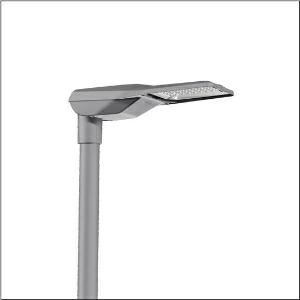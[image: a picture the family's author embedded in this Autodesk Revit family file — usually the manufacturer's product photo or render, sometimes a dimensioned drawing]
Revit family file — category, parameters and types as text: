
# Revit family: streetlight_sl_21_iq_mini___st0_5a_5xe2b41g08gb_465e
name_source: partatom
category: Lighting Fixtures
units: mm (PartAtom-declared; Revit-internal decimal feet)

## family parameters
Cut with Voids When Loaded = No
Host = Face
Light Source = No
Part Type = Normal
Room Calculation Point = No
Round Connector Dimension = Use Diameter
Shared = No

## types (1)
- --- (1 x LED, 5920 lm, 37.1 W, 4000K)
    Apparent Load = 37 VA
    CIE Flux Codes = 41 75 97 100 100
    Color Rendering = 70
    Color Temperature = 4000K
    Default Elevation = 1800 mm
    Description = Streetlight SL 21 iQ mini, mast luminaire, primary light control with lens, of PMMA, primary optical cover: cover, of toughened safety glass, transparent, light distribution: ST0.5a, light emission: direct distribution, primary light characteristic: asymmetric, installation type: post-top, side-entry, LED, High Power LED, rated luminous flux: 5.920lm, luminous efficacy: 160lm/W, light colour: 740, colour temperature: 4000K, control: Street-Remote, Auto-Match, Temp-Guard, Lumen-Switch, Night-Set, Smart-Wire, Light-Fading, Desk-Remote (wireless, voltage-free reading and setting of iQ features in the workshop via application-optimized NFC function/RFID function), optimised constant luminous flux control (CLO 2.0), presetting dimming linear, mains connection: 220..240V, AC, 50/60Hz, start of lifetime: 37W, end of service life: 39W, reduction: 18W, luminaire housing, of diecast aluminium, powder-coated, Siteco® metallic grey (DB 702S), corrosivity category C5 mid according to DIN EN ISO 12944, please order mast flange separately, inclination adjustable: 0°, 5°, 10°, 15°, sealing non-destructively replaceable, multi-level sealing system, length: 628mm, width: 235mm, height: 110mm, mast flange for spigot size: 42mm (side-entry): 5XC10008XM4, 60/48mm (side-entry/post-top): 5XC10108XM2, 76/60mm (side-entry/post-top): 5XC10108XM1, protection rating (complete): IP66, insulation class (complete): insulation class II (safety insulation), certification: CE, ENEC, ENEC+, VDE, impact resistance: IK09, permissible operating ambient temperature for outdoor applications: -40..+50°C, standard-compliant lighting for roads and squares, packaging unit: 1 piece

Light Distribution: ST0.5a
    Height = 110 mm
    Lamp = 1 x LED
    Lamp Light Flux = 5920 lm
    Lamp Power = 37.1 W
    Lamp count = 1
    Length = 625 mm
    Luminous efficacy = 160 lm/W
    Manufacturer = Siteco
    ModVariant = No
    Model = 5XE2B41G08GB
    Number of Poles = 1
    OnlyDefault = Yes
    Power Factor = 1
    Product Name = Streetlight SL 21 iQ mini | ST0.5a
    Product group = mast luminaire | pylon top
    ProductGroupID = 6100
    Protection Class = Protection class II
    Protection Degree = IP 66
    RLX_Detail_Level = 1
    RLX_Emergency_Light_Flux = 0 lm
    RLX_Emergency_Type = 0
    RLX_Emergency_Type_DB = No
    RlxData = <blob elided: 103353 chars, md5=882ffc48>
    Socket = socket
    Standby Power = 0 W
    System Light Flux = 5920 lm
    System Power = 37 W
    Type Comments = factory setting: luminous flux: 100 % | dim-lin: 254 | 385 mA
    Type Image = l_1003519.jpg
    URL = http://relux.com
    VarID = @adj_143775
    Voltage = 0 V
    Weight = 0.00 kg
    Width = 234 mm

## geometry (parser evidence)
native form markers: Blend x4, Sweep x11
no freeform markers — native parametric forms only
